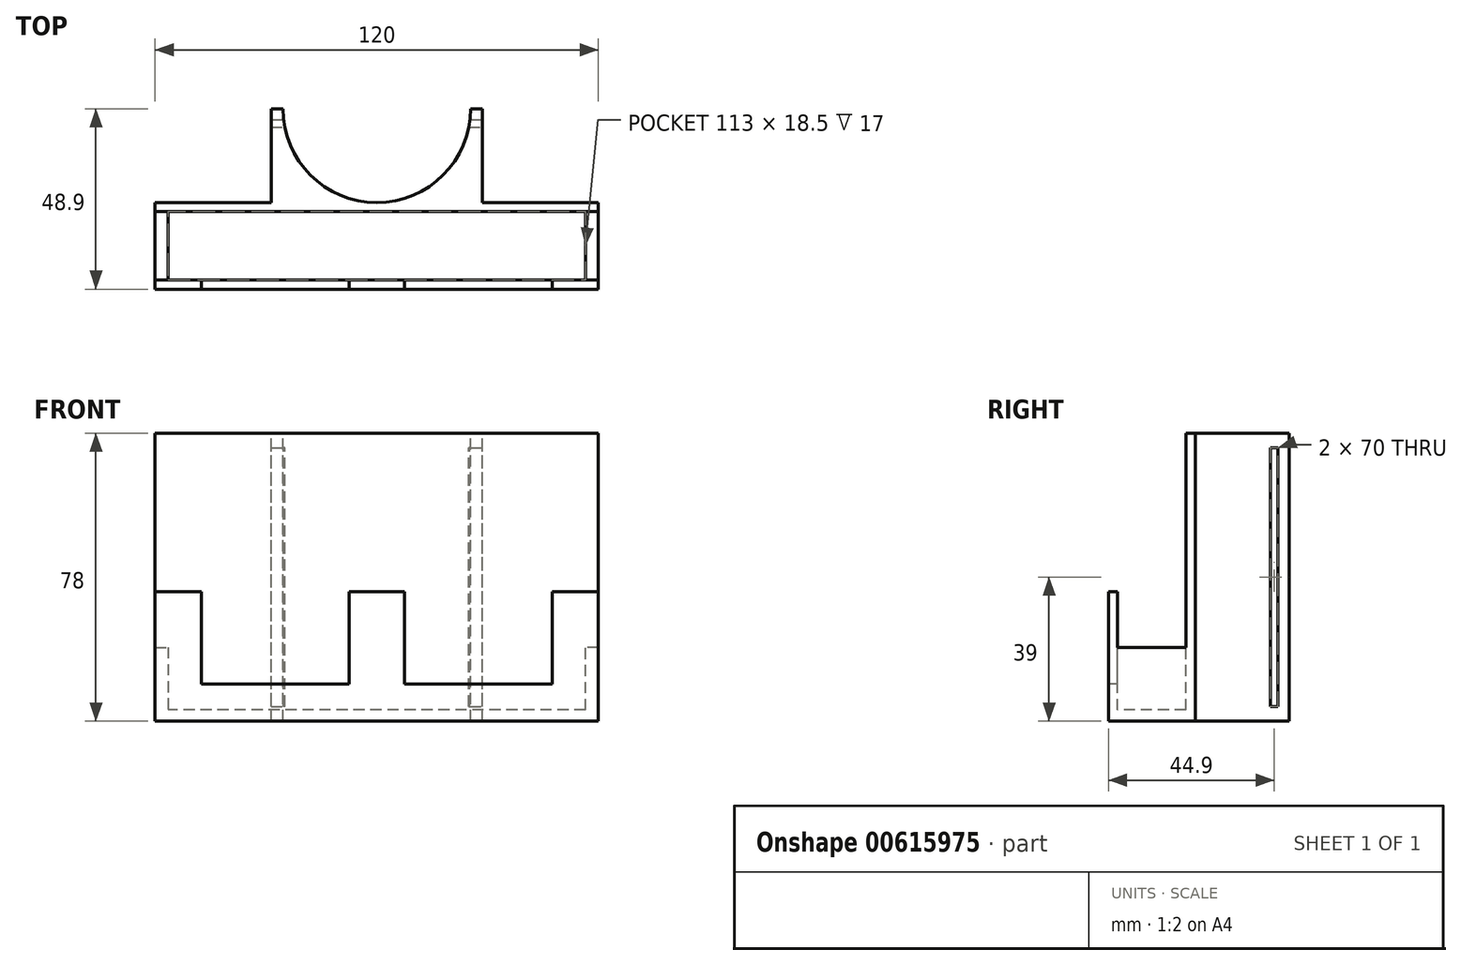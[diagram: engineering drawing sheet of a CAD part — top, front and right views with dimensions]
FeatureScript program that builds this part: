
annotation { "Feature Type Name" : "Feature", "Feature Type Description" : "" }
export const myFeature = defineFeature(function(context is Context, id is Id, definition is map)
    precondition{}
    {
        {
            var Q0;
            Q0=qCreatedBy(makeId("Front.planeOp"),FACE);
            var sketch = newSketch(context, id + "F0", { "sketchPlane" : qUnion([Q0])});
            skLineSegment(sketch, "E0.bottom", {"start": v(57.5, 37.5) * mm, "end": v(-57.5, 37.5) * mm});
            skLineSegment(sketch, "E0.top", {"start": v(57.5, -37.5) * mm, "end": v(-57.5, -37.5) * mm});
            skLineSegment(sketch, "E0.left", {"start": v(57.5, 37.5) * mm, "end": v(57.5, -37.5) * mm});
            skLineSegment(sketch, "E0.right", {"start": v(-57.5, 37.5) * mm, "end": v(-57.5, -37.5) * mm});
            skPoint(sketch, "E0.middle", {"position": v(0, 0) * mm});
            skSolve(sketch);
        }
        {
            var Q0;
            Q0=makeQuery(id+"F0.imprint","IMPRINT",FACE,{"disambiguationData":[TD([[makeQuery(id+"F0.imprint","IMPRINT",EDGE,{"derivedFrom":sQuery(id+"F0.wireOp",EDGE,"E0.bottom")}),1.0]])]});
            extrude(context, id + "F1", {"entities" : qUnion([Q0]), "oppositeDirection" : true, "depth" : 2.5 * mm, "offsetDistance" : 25 * mm});
        }
        {
            var Q0;
            Q0=makeQuery(id+"F1.opExtrude","SWEPT_FACE",FACE,{"disambiguationData":[OSD([sQuery(id+"F0.wireOp",EDGE,"E0.top")])]});
            var sketch = newSketch(context, id + "F2", { "sketchPlane" : qUnion([Q0])});
            skLineSegment(sketch, "E1.bottom", {"start": v(-57.5, -2.5) * mm, "end": v(57.5, -2.5) * mm});
            skLineSegment(sketch, "E1.top", {"start": v(-57.5, 21) * mm, "end": v(57.5, 21) * mm});
            skLineSegment(sketch, "E1.left", {"start": v(-57.5, -2.5) * mm, "end": v(-57.5, 21) * mm});
            skLineSegment(sketch, "E1.right", {"start": v(57.5, -2.5) * mm, "end": v(57.5, 21) * mm});
            skSolve(sketch);
        }
        {
            var Q0;
            Q0=qSketchRegion(id+"F2",true);
            extrude(context, id + "F3", {"entities" : qUnion([Q0]), "operationType" : NewBodyOperationType.ADD, "depth" : 3 * mm, "offsetDistance" : 25 * mm});
        }
        {
            var Q0;
            Q0=makeQuery(id+"F3.opExtrude","SWEPT_FACE",FACE,{"disambiguationData":[OSD([sQuery(id+"F2.wireOp",EDGE,"E1.top")])]});
            var sketch = newSketch(context, id + "F4", { "sketchPlane" : qUnion([Q0])});
            skLineSegment(sketch, "E2.bottom", {"start": v(-57.5, -40.5) * mm, "end": v(-47.5, -40.5) * mm});
            skLineSegment(sketch, "E2.top", {"start": v(-57.5, -5.5) * mm, "end": v(-47.5, -5.5) * mm});
            skLineSegment(sketch, "E2.left", {"start": v(-57.5, -40.5) * mm, "end": v(-57.5, -5.5) * mm});
            skLineSegment(sketch, "E2.right", {"start": v(-47.5, -40.5) * mm, "end": v(-47.5, -5.5) * mm});
            skLineSegment(sketch, "E3.bottom", {"start": v(57.5, -40.5) * mm, "end": v(47.5, -40.5) * mm});
            skLineSegment(sketch, "E3.top", {"start": v(57.5, -5.5) * mm, "end": v(47.5, -5.5) * mm});
            skLineSegment(sketch, "E3.left", {"start": v(57.5, -40.5) * mm, "end": v(57.5, -5.5) * mm});
            skLineSegment(sketch, "E3.right", {"start": v(47.5, -40.5) * mm, "end": v(47.5, -5.5) * mm});
            skLineSegment(sketch, "E4.bottom", {"start": v(0, -40.5) * mm, "end": v(7.5, -40.5) * mm});
            skLineSegment(sketch, "E4.top", {"start": v(0, -5.5) * mm, "end": v(7.5, -5.5) * mm});
            skLineSegment(sketch, "E4.left", {"start": v(0, -40.5) * mm, "end": v(0, -5.5) * mm});
            skLineSegment(sketch, "E4.right", {"start": v(7.5, -40.5) * mm, "end": v(7.5, -5.5) * mm});
            skLineSegment(sketch, "E5.bottom", {"start": v(0, -40.5) * mm, "end": v(-7.5, -40.5) * mm});
            skLineSegment(sketch, "E5.top", {"start": v(0, -5.5) * mm, "end": v(-7.5, -5.5) * mm});
            skLineSegment(sketch, "E5.right", {"start": v(-7.5, -40.5) * mm, "end": v(-7.5, -5.5) * mm});
            skLineSegment(sketch, "E6.bottom", {"start": v(-47.5, -40.5) * mm, "end": v(-7.5, -40.5) * mm});
            skLineSegment(sketch, "E6.top", {"start": v(-47.5, -30.5) * mm, "end": v(-7.5, -30.5) * mm});
            skLineSegment(sketch, "E6.left", {"start": v(-47.5, -40.5) * mm, "end": v(-47.5, -30.5) * mm});
            skLineSegment(sketch, "E6.right", {"start": v(-7.5, -40.5) * mm, "end": v(-7.5, -30.5) * mm});
            skLineSegment(sketch, "E7.bottom", {"start": v(7.5, -40.5) * mm, "end": v(47.5, -40.5) * mm});
            skLineSegment(sketch, "E7.top", {"start": v(7.5, -30.5) * mm, "end": v(47.5, -30.5) * mm});
            skLineSegment(sketch, "E7.left", {"start": v(7.5, -40.5) * mm, "end": v(7.5, -30.5) * mm});
            skLineSegment(sketch, "E7.right", {"start": v(47.5, -40.5) * mm, "end": v(47.5, -30.5) * mm});
            skSolve(sketch);
        }
        {
            var Q0;
            Q0=qSketchRegion(id+"F4",true);
            extrude(context, id + "F5", {"entities" : qUnion([Q0]), "operationType" : NewBodyOperationType.ADD, "oppositeDirection" : true, "depth" : 2.5 * mm, "offsetDistance" : 25 * mm});
        }
        {
            var Q0;
            Q0=makeQuery(id+"F5.boolean.opBoolean","MERGE",FACE,{"derivedFrom":[makeQuery(id+"F3.boolean.opBoolean","MERGE",FACE,{"derivedFrom":[makeQuery(id+"F1.opExtrude","SWEPT_FACE",FACE,{"disambiguationData":[OSD([sQuery(id+"F0.wireOp",EDGE,"E0.right")])]}),makeQuery(id+"F3.opExtrude","SWEPT_FACE",FACE,{"disambiguationData":[OSD([sQuery(id+"F2.wireOp",EDGE,"E1.left")])]})]}),makeQuery(id+"F5.opExtrude","SWEPT_FACE",FACE,{"disambiguationData":[OSD([sQuery(id+"F4.wireOp",EDGE,"E2.left")])]})]});
            var sketch = newSketch(context, id + "F6", { "sketchPlane" : qUnion([Q0])});
            skLineSegment(sketch, "E8.bottom", {"start": v(-2.5, -40.5) * mm, "end": v(21, -40.5) * mm});
            skLineSegment(sketch, "E8.top", {"start": v(-2.5, -20.5) * mm, "end": v(21, -20.5) * mm});
            skLineSegment(sketch, "E8.left", {"start": v(-2.5, -40.5) * mm, "end": v(-2.5, -20.5) * mm});
            skLineSegment(sketch, "E8.right", {"start": v(21, -40.5) * mm, "end": v(21, -20.5) * mm});
            skSolve(sketch);
        }
        {
            var Q0;
            Q0=qSketchRegion(id+"F6",true);
            extrude(context, id + "F7", {"entities" : qUnion([Q0]), "operationType" : NewBodyOperationType.ADD, "depth" : 2.5 * mm, "offsetDistance" : 25 * mm});
        }
        {
            var Q0;
            Q0=makeQuery(id+"F5.boolean.opBoolean","MERGE",FACE,{"derivedFrom":[makeQuery(id+"F3.boolean.opBoolean","MERGE",FACE,{"derivedFrom":[makeQuery(id+"F1.opExtrude","SWEPT_FACE",FACE,{"disambiguationData":[OSD([sQuery(id+"F0.wireOp",EDGE,"E0.left")])]}),makeQuery(id+"F3.opExtrude","SWEPT_FACE",FACE,{"disambiguationData":[OSD([sQuery(id+"F2.wireOp",EDGE,"E1.right")])]})]}),makeQuery(id+"F5.opExtrude","SWEPT_FACE",FACE,{"disambiguationData":[OSD([sQuery(id+"F4.wireOp",EDGE,"E3.left")])]})]});
            var sketch = newSketch(context, id + "F8", { "sketchPlane" : qUnion([Q0])});
            skLineSegment(sketch, "E9.bottom", {"start": v(-21, -40.5) * mm, "end": v(2.5, -40.5) * mm});
            skLineSegment(sketch, "E9.top", {"start": v(-21, -20.5) * mm, "end": v(2.5, -20.5) * mm});
            skLineSegment(sketch, "E9.left", {"start": v(-21, -40.5) * mm, "end": v(-21, -20.5) * mm});
            skLineSegment(sketch, "E9.right", {"start": v(2.5, -40.5) * mm, "end": v(2.5, -20.5) * mm});
            skSolve(sketch);
        }
        {
            var Q0;
            Q0=qSketchRegion(id+"F8",true);
            extrude(context, id + "F9", {"entities" : qUnion([Q0]), "operationType" : NewBodyOperationType.ADD, "depth" : 2.5 * mm, "offsetDistance" : 25 * mm});
        }
        {
            var Q0;
            {var subQ1=sQuery(id+"F4.wireOp",EDGE,"E3.left");Q0=makeQuery(id+"F9.boolean.opBoolean","SPLIT",FACE,{"disambiguationData":[TD([makeQuery(id+"F3.opExtrude","SWEPT_FACE",FACE,{"disambiguationData":[OSD([sQuery(id+"F2.wireOp",EDGE,"E1.top")])]})])],"derivedFrom":makeQuery(id+"F5.boolean.opBoolean","MERGE",FACE,{"derivedFrom":[makeQuery(id+"F3.boolean.opBoolean","MERGE",FACE,{"derivedFrom":[makeQuery(id+"F1.opExtrude","SWEPT_FACE",FACE,{"disambiguationData":[OSD([sQuery(id+"F0.wireOp",EDGE,"E0.left")])]}),makeQuery(id+"F3.opExtrude","SWEPT_FACE",FACE,{"disambiguationData":[OSD([sQuery(id+"F2.wireOp",EDGE,"E1.right")])]})]}),makeQuery(id+"F5.opExtrude","SWEPT_FACE",FACE,{"disambiguationData":[OSD([subQ1])]})]})});}
            var sketch = newSketch(context, id + "F10", { "sketchPlane" : qUnion([Q0])});
            skLineSegment(sketch, "E10.bottom", {"start": v(-21, -5.5) * mm, "end": v(-18.5, -5.5) * mm});
            skLineSegment(sketch, "E10.top", {"start": v(-21, -20.5) * mm, "end": v(-18.5, -20.5) * mm});
            skLineSegment(sketch, "E10.left", {"start": v(-21, -5.5) * mm, "end": v(-21, -20.5) * mm});
            skLineSegment(sketch, "E10.right", {"start": v(-18.5, -5.5) * mm, "end": v(-18.5, -20.5) * mm});
            skLineSegment(sketch, "E11.bottom", {"start": v(0, -20.5) * mm, "end": v(2.5, -20.5) * mm});
            skLineSegment(sketch, "E11.top", {"start": v(0, 37.5) * mm, "end": v(2.5, 37.5) * mm});
            skLineSegment(sketch, "E11.left", {"start": v(0, -20.5) * mm, "end": v(0, 37.5) * mm});
            skLineSegment(sketch, "E11.right", {"start": v(2.5, -20.5) * mm, "end": v(2.5, 37.5) * mm});
            skSolve(sketch);
        }
        {
            var Q0;
            Q0=qSketchRegion(id+"F10",true);
            extrude(context, id + "F11", {"entities" : qUnion([Q0]), "operationType" : NewBodyOperationType.ADD, "depth" : 2.5 * mm, "offsetDistance" : 25 * mm});
        }
        {
            var Q0;
            {var subQ2=sQuery(id+"F4.wireOp",EDGE,"E2.left");Q0=makeQuery(id+"F7.boolean.opBoolean","SPLIT",FACE,{"disambiguationData":[TD([makeQuery(id+"F3.opExtrude","SWEPT_FACE",FACE,{"disambiguationData":[OSD([sQuery(id+"F2.wireOp",EDGE,"E1.top")])]})])],"derivedFrom":makeQuery(id+"F5.boolean.opBoolean","MERGE",FACE,{"derivedFrom":[makeQuery(id+"F3.boolean.opBoolean","MERGE",FACE,{"derivedFrom":[makeQuery(id+"F1.opExtrude","SWEPT_FACE",FACE,{"disambiguationData":[OSD([sQuery(id+"F0.wireOp",EDGE,"E0.right")])]}),makeQuery(id+"F3.opExtrude","SWEPT_FACE",FACE,{"disambiguationData":[OSD([sQuery(id+"F2.wireOp",EDGE,"E1.left")])]})]}),makeQuery(id+"F5.opExtrude","SWEPT_FACE",FACE,{"disambiguationData":[OSD([subQ2])]})]})});}
            var sketch = newSketch(context, id + "F12", { "sketchPlane" : qUnion([Q0])});
            skLineSegment(sketch, "E12.bottom", {"start": v(21, -20.5) * mm, "end": v(18.5, -20.5) * mm});
            skLineSegment(sketch, "E12.top", {"start": v(21, -5.5) * mm, "end": v(18.5, -5.5) * mm});
            skLineSegment(sketch, "E12.left", {"start": v(21, -20.5) * mm, "end": v(21, -5.5) * mm});
            skLineSegment(sketch, "E12.right", {"start": v(18.5, -20.5) * mm, "end": v(18.5, -5.5) * mm});
            skLineSegment(sketch, "E13.bottom", {"start": v(0, -20.5) * mm, "end": v(-2.5, -20.5) * mm});
            skLineSegment(sketch, "E13.top", {"start": v(0, 37.5) * mm, "end": v(-2.5, 37.5) * mm});
            skLineSegment(sketch, "E13.left", {"start": v(0, -20.5) * mm, "end": v(0, 37.5) * mm});
            skLineSegment(sketch, "E13.right", {"start": v(-2.5, -20.5) * mm, "end": v(-2.5, 37.5) * mm});
            skSolve(sketch);
        }
        {
            var Q0;
            Q0=qSketchRegion(id+"F12",true);
            extrude(context, id + "F13", {"entities" : qUnion([Q0]), "operationType" : NewBodyOperationType.ADD, "depth" : 2.5 * mm, "offsetDistance" : 25 * mm});
        }
        {
            var Q0;
            Q0=makeQuery(id+"F13.boolean.opBoolean","MERGE",FACE,{"derivedFrom":[makeQuery(id+"F11.boolean.opBoolean","MERGE",FACE,{"derivedFrom":[makeQuery(id+"F9.boolean.opBoolean","MERGE",FACE,{"derivedFrom":[makeQuery(id+"F7.boolean.opBoolean","MERGE",FACE,{"derivedFrom":[makeQuery(id+"F3.boolean.opBoolean","MERGE",FACE,{"derivedFrom":[makeQuery(id+"F1.opExtrude","CAP_FACE",FACE,{"disambiguationData":[OSD([sQuery(id+"F0.wireOp",EDGE,"E0.bottom"),sQuery(id+"F0.wireOp",EDGE,"E0.top"),sQuery(id+"F0.wireOp",EDGE,"E0.left"),sQuery(id+"F0.wireOp",EDGE,"E0.right")])],"isStart":false}),makeQuery(id+"F3.opExtrude","SWEPT_FACE",FACE,{"disambiguationData":[OSD([sQuery(id+"F2.wireOp",EDGE,"E1.bottom")])]})]}),makeQuery(id+"F7.opExtrude","SWEPT_FACE",FACE,{"disambiguationData":[OSD([sQuery(id+"F6.wireOp",EDGE,"E8.left")])]})]}),makeQuery(id+"F9.opExtrude","SWEPT_FACE",FACE,{"disambiguationData":[OSD([sQuery(id+"F8.wireOp",EDGE,"E9.right")])]})]}),makeQuery(id+"F11.opExtrude","SWEPT_FACE",FACE,{"disambiguationData":[OSD([sQuery(id+"F10.wireOp",EDGE,"E11.right")])]})]}),makeQuery(id+"F13.opExtrude","SWEPT_FACE",FACE,{"disambiguationData":[OSD([sQuery(id+"F12.wireOp",EDGE,"E13.right")])]})]});
            var sketch = newSketch(context, id + "F14", { "sketchPlane" : qUnion([Q0])});
            skLineSegment(sketch, "E14.bottom", {"start": v(28.58, -40.5) * mm, "end": v(-28.58, -40.5) * mm});
            skLineSegment(sketch, "E14.top", {"start": v(28.58, 37.5) * mm, "end": v(-28.58, 37.5) * mm});
            skLineSegment(sketch, "E14.left", {"start": v(28.58, -40.5) * mm, "end": v(28.58, 37.5) * mm});
            skLineSegment(sketch, "E14.right", {"start": v(-28.58, -40.5) * mm, "end": v(-28.58, 37.5) * mm});
            skPoint(sketch, "E14.middle", {"position": v(0, -1.5) * mm});
            skPoint(sketch, "E14.middle.positionSnap0", {"position": v(-60, -1.5) * mm});
            skPoint(sketch, "E14.centerSnap0", {"position": v(-60, -1.5) * mm});
            skSolve(sketch);
        }
        {
            var Q0;
            Q0=qSketchRegion(id+"F14",true);
            extrude(context, id + "F15", {"entities" : qUnion([Q0]), "operationType" : NewBodyOperationType.ADD, "depth" : 25.4 * mm, "offsetDistance" : 25 * mm});
        }
        {
            var Q0;
            Q0=makeQuery(id+"F15.boolean.opBoolean","MERGE",FACE,{"derivedFrom":[makeQuery(id+"F13.boolean.opBoolean","MERGE",FACE,{"derivedFrom":[makeQuery(id+"F11.boolean.opBoolean","MERGE",FACE,{"derivedFrom":[makeQuery(id+"F1.opExtrude","SWEPT_FACE",FACE,{"disambiguationData":[OSD([sQuery(id+"F0.wireOp",EDGE,"E0.bottom")])]}),makeQuery(id+"F11.opExtrude","SWEPT_FACE",FACE,{"disambiguationData":[OSD([sQuery(id+"F10.wireOp",EDGE,"E11.top")])]})]}),makeQuery(id+"F13.opExtrude","SWEPT_FACE",FACE,{"disambiguationData":[OSD([sQuery(id+"F12.wireOp",EDGE,"E13.top")])]})]}),makeQuery(id+"F15.opExtrude","SWEPT_FACE",FACE,{"disambiguationData":[OSD([sQuery(id+"F14.wireOp",EDGE,"E14.top")])]})]});
            var sketch = newSketch(context, id + "F16", { "sketchPlane" : qUnion([Q0])});
            skCircle(sketch, "E15", {"center": v(0, 27.9) * mm, "radius": 25.4 * mm});
            skSolve(sketch);
        }
        {
            var Q0;
            Q0=qSketchRegion(id+"F16",true);
            extrude(context, id + "F17", {"entities" : qUnion([Q0]), "operationType" : NewBodyOperationType.REMOVE, "oppositeDirection" : true, "depth" : 78 * mm, "offsetDistance" : 25 * mm});
        }
        {
            var Q0;
            Q0=makeQuery(id+"F15.opExtrude","SWEPT_FACE",FACE,{"disambiguationData":[OSD([sQuery(id+"F14.wireOp",EDGE,"E14.right")])]});
            var sketch = newSketch(context, id + "F18", { "sketchPlane" : qUnion([Q0])});
            skLineSegment(sketch, "E16.bottom", {"start": v(22.9, -36.5) * mm, "end": v(24.9, -36.5) * mm});
            skLineSegment(sketch, "E16.top", {"start": v(22.9, 33.5) * mm, "end": v(24.9, 33.5) * mm});
            skLineSegment(sketch, "E16.left", {"start": v(22.9, -36.5) * mm, "end": v(22.9, 33.5) * mm});
            skLineSegment(sketch, "E16.right", {"start": v(24.9, -36.5) * mm, "end": v(24.9, 33.5) * mm});
            skSolve(sketch);
        }
        {
            var Q0;
            Q0=qSketchRegion(id+"F6",true);
            extrude(context, id + "F19", {"entities" : qUnion([Q0]), "operationType" : NewBodyOperationType.ADD, "oppositeDirection" : true, "depth" : 1 * mm, "offsetDistance" : 25 * mm});
        }
        {
            var Q0;
            Q0=qSketchRegion(id+"F8",true);
            extrude(context, id + "F20", {"entities" : qUnion([Q0]), "operationType" : NewBodyOperationType.ADD, "oppositeDirection" : true, "depth" : 1 * mm, "offsetDistance" : 25 * mm});
        }
        {
            var Q0;
            Q0=makeQuery(id+"F18.imprint","IMPRINT",FACE,{"disambiguationData":[TD([[makeQuery(id+"F18.imprint","IMPRINT",EDGE,{"derivedFrom":sQuery(id+"F18.wireOp",EDGE,"E16.bottom")}),1.0]])]});
            extrude(context, id + "F21", {"entities" : qUnion([Q0]), "operationType" : NewBodyOperationType.REMOVE, "oppositeDirection" : true, "depth" : 57.15 * mm, "offsetDistance" : 25 * mm});
        }
    });
